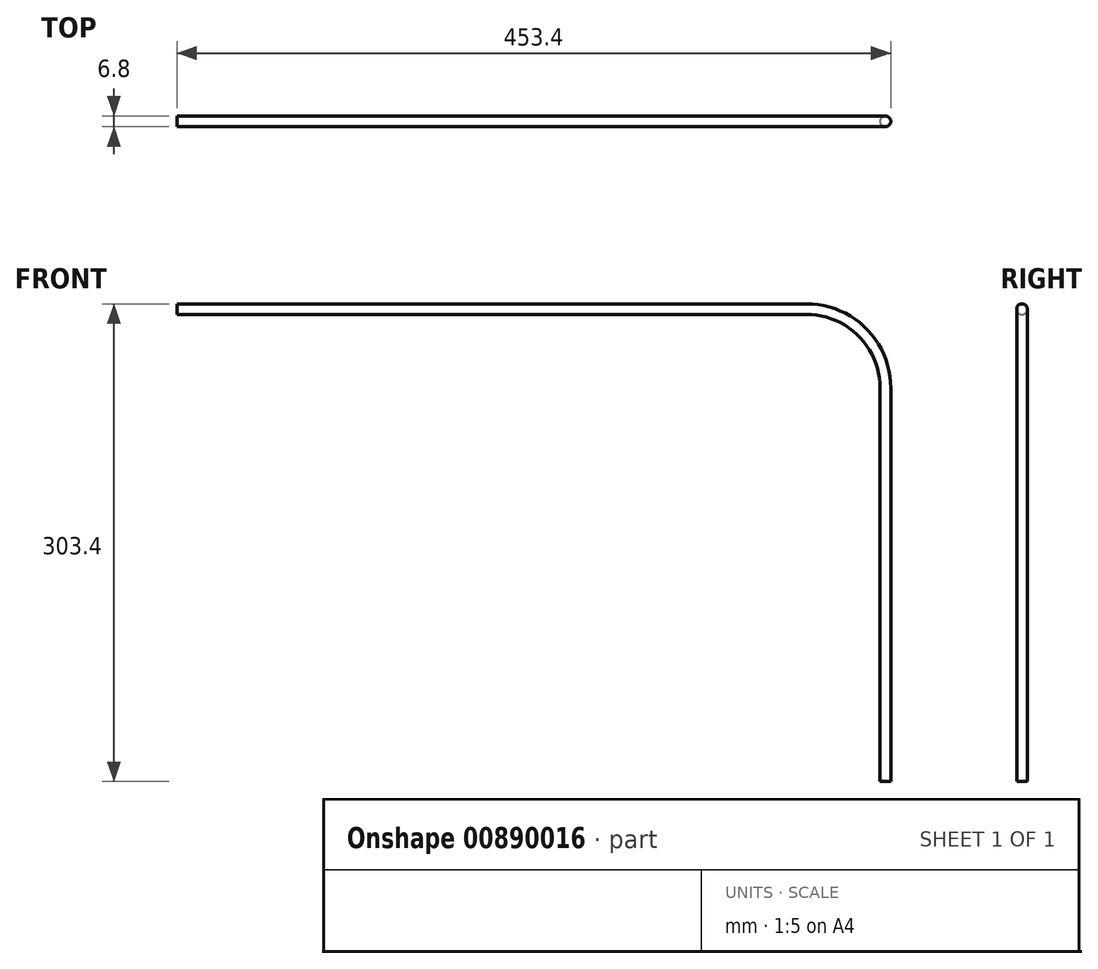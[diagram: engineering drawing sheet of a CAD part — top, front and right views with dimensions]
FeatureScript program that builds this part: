
annotation { "Feature Type Name" : "Feature", "Feature Type Description" : "" }
export const myFeature = defineFeature(function(context is Context, id is Id, definition is map)
    precondition{}
    {
        {
            var Q0;
            Q0=qCreatedBy(makeId("Front.planeOp"),FACE);
            var sketch = newSketch(context, id + "F0", { "sketchPlane" : qUnion([Q0])});
            skLineSegment(sketch, "E0", {"start": v(0, 0) * mm, "end": v(0, 250) * mm});
            skLineSegment(sketch, "E1", {"start": v(-50, 300) * mm, "end": v(-450, 300) * mm});
            skPoint(sketch, "E2.visualSharp", {"position": v(0, 300) * mm});
            skArc(sketch, "E2.filletArc", {"start": v(0, 250) * mm, "mid": v(-14.64, 285.36) * mm, "end": v(-50, 300) * mm});
            skSolve(sketch);
        }
        {
            var Q0;
            Q0=qCreatedBy(makeId("Top.planeOp"),FACE);
            var sketch = newSketch(context, id + "F1", { "sketchPlane" : qUnion([Q0])});
            skCircle(sketch, "E3", {"center": v(0, 0) * mm, "radius": 3.4 * mm});
            skSolve(sketch);
        }
        {
            var Q0;
            Q0=makeQuery(id+"F1.imprint","IMPRINT",FACE,{"disambiguationData":[TD([[makeQuery(id+"F1.imprint","IMPRINT",EDGE,{"derivedFrom":sQuery(id+"F1.wireOp",EDGE,"E3")}),1.0]])]});
            var Q1;
            Q1=sQuery(id+"F0.wireOp",EDGE,"E1");
            var Q2;
            Q2=sQuery(id+"F0.wireOp",EDGE,"E2.filletArc");
            var Q3;
            Q3=sQuery(id+"F0.wireOp",EDGE,"E0");
            sweep(context, id + "F2", {"profiles" : qUnion([Q0]), "path" : qUnion([Q1, Q2, Q3])});
        }
    });
